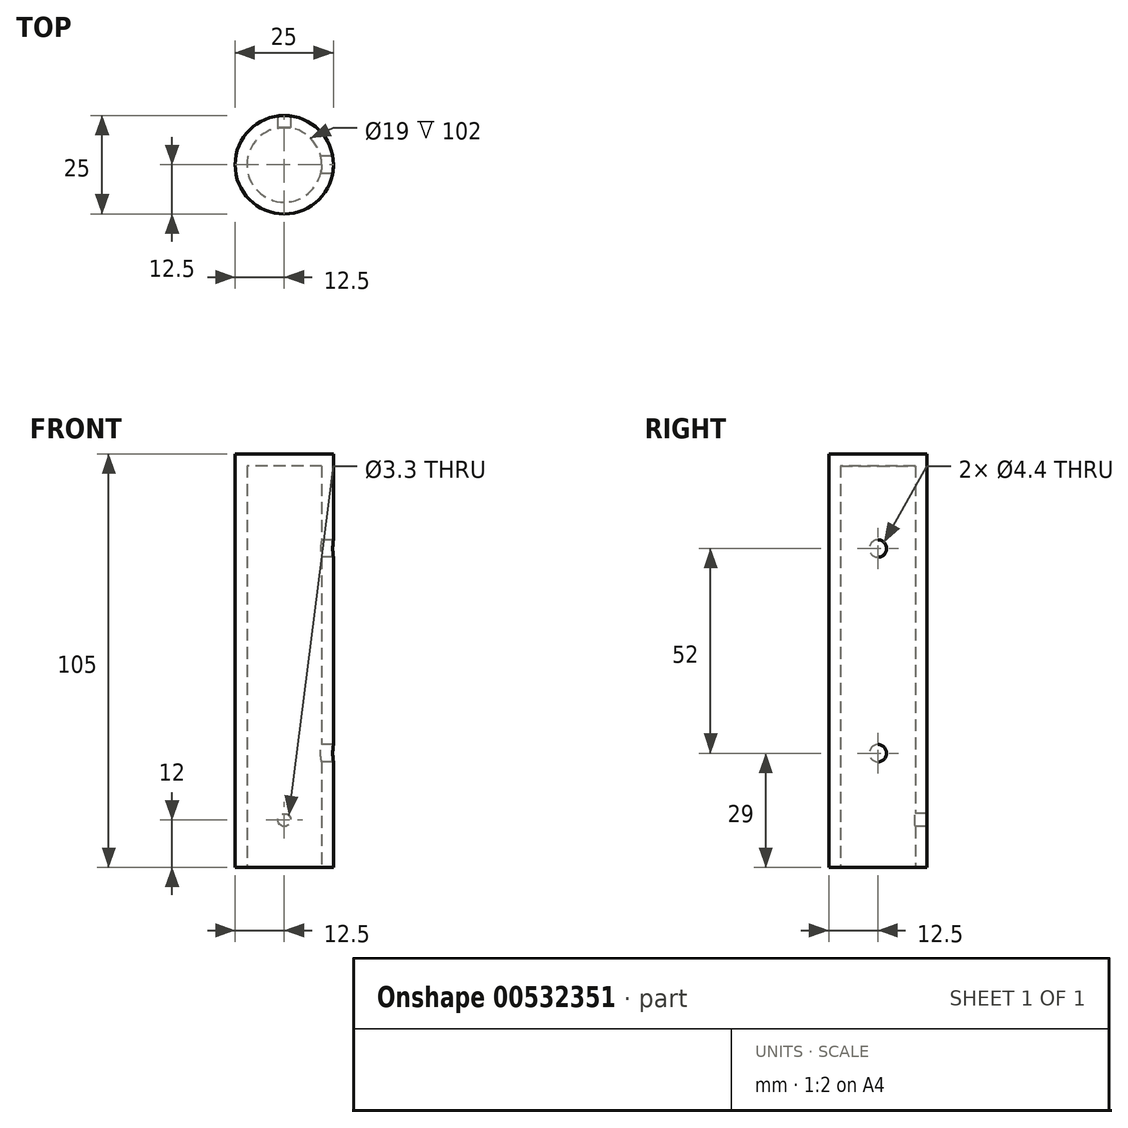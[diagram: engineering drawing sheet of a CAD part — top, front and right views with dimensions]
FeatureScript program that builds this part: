
annotation { "Feature Type Name" : "Feature", "Feature Type Description" : "" }
export const myFeature = defineFeature(function(context is Context, id is Id, definition is map)
    precondition{}
    {
        {
            var Q0;
            Q0=qCreatedBy(makeId("Top.planeOp"),FACE);
            var sketch = newSketch(context, id + "F0", { "sketchPlane" : qUnion([Q0])});
            skCircle(sketch, "E0", {"center": v(0, 0) * mm, "radius": 12.5 * mm});
            skCircle(sketch, "E1.0", {"center": v(0, 0) * mm, "radius": 9.5 * mm});
            skSolve(sketch);
        }
        {
            var Q0;
            Q0=qSketchRegion(id+"F0",true);
            extrude(context, id + "F1", {"entities" : qUnion([Q0]), "depth" : 105 * mm});
        }
        {
            var Q0;
            Q0=makeQuery(id+"F1.opExtrude","CAP_FACE",FACE,{"disambiguationData":[OSD([sQuery(id+"F0.wireOp",EDGE,"E0"),sQuery(id+"F0.wireOp",EDGE,"E1.0")])],"isStart":false});
            var sketch = newSketch(context, id + "F2", { "sketchPlane" : qUnion([Q0])});
            skCircle(sketch, "E2.0", {"center": v(0, 0) * mm, "radius": 12.5 * mm});
            skSolve(sketch);
        }
        {
            var Q0;
            Q0=qSketchRegion(id+"F2",true);
            extrude(context, id + "F3", {"entities" : qUnion([Q0]), "operationType" : NewBodyOperationType.ADD, "oppositeDirection" : true, "depth" : 3 * mm});
        }
        {
            var Q0;
            Q0=qCreatedBy(makeId("Front.planeOp"),FACE);
            var sketch = newSketch(context, id + "F4", { "sketchPlane" : qUnion([Q0])});
            skPoint(sketch, "E3", {"position": v(0, 12) * mm});
            skSolve(sketch);
        }
        {
            var Q0;
            Q0=sQuery(id+"F4.wireOp",VERTEX,"E3");
            var Q1;
            Q1=makeQuery(id+"F1.opExtrude","SWEPT_BODY",BODY,{"disambiguationData":[OSD([sQuery(id+"F0.wireOp",EDGE,"E0"),sQuery(id+"F0.wireOp",EDGE,"E1.0")])]});
            hole(context, id + "F5", {"style" : HoleStyle.SIMPLE, "endStyle" : HoleEndStyle.BLIND, "standardTappedOrClearance" : lookupTablePath({ "standard" : "ISO", "engagement" : "75%", "pitch" : "0.7 mm", "size" : "M4", "type" : "Tapped" }), "standardBlindInLast" : lookupTablePath({ "standard" : "ISO", "engagement" : "75%", "pitch" : "0.7 mm", "size" : "M4", "type" : "Tapped" }), "holeDiameter" : 3.3 * mm, "showTappedDepth" : true, "holeDepth" : 22.1 * mm, "isTappedThrough" : true, "tappedDepth" : 20 * mm, "tapClearance" : 3, "locations" : qUnion([Q0]), "scope" : qUnion([Q1]), "majorDiameter" : 4 * mm});
        }
        {
            var Q0;
            Q0=qCreatedBy(makeId("Right.planeOp"),FACE);
            var sketch = newSketch(context, id + "F6", { "sketchPlane" : qUnion([Q0])});
            skPoint(sketch, "E4", {"position": v(0, 81) * mm});
            skPoint(sketch, "E5", {"position": v(0, 29) * mm});
            skSolve(sketch);
        }
        {
            var Q0;
            Q0=sQuery(id+"F6.wireOp",VERTEX,"E4");
            var Q1;
            Q1=sQuery(id+"F6.wireOp",VERTEX,"E5");
            var Q2;
            Q2=makeQuery(id+"F1.opExtrude","SWEPT_BODY",BODY,{"disambiguationData":[OSD([sQuery(id+"F0.wireOp",EDGE,"E0"),sQuery(id+"F0.wireOp",EDGE,"E1.0")])]});
            hole(context, id + "F7", {"style" : HoleStyle.SIMPLE, "endStyle" : HoleEndStyle.BLIND, "oppositeDirection" : true, "standardTappedOrClearance" : lookupTablePath({ "standard" : "ISO", "fit" : "Normal", "size" : "M4", "type" : "Clearance" }), "standardBlindInLast" : lookupTablePath({ "fit" : "Standard", "standard" : "ISO", "size" : "M4", "type" : "Clearance" }), "holeDiameter" : 4.4 * mm, "holeDepth" : 22.1 * mm, "isTappedThrough" : true, "tappedDepth" : 20 * mm, "tapClearance" : 3, "locations" : qUnion([Q0, Q1]), "scope" : qUnion([Q2])});
        }
    });
